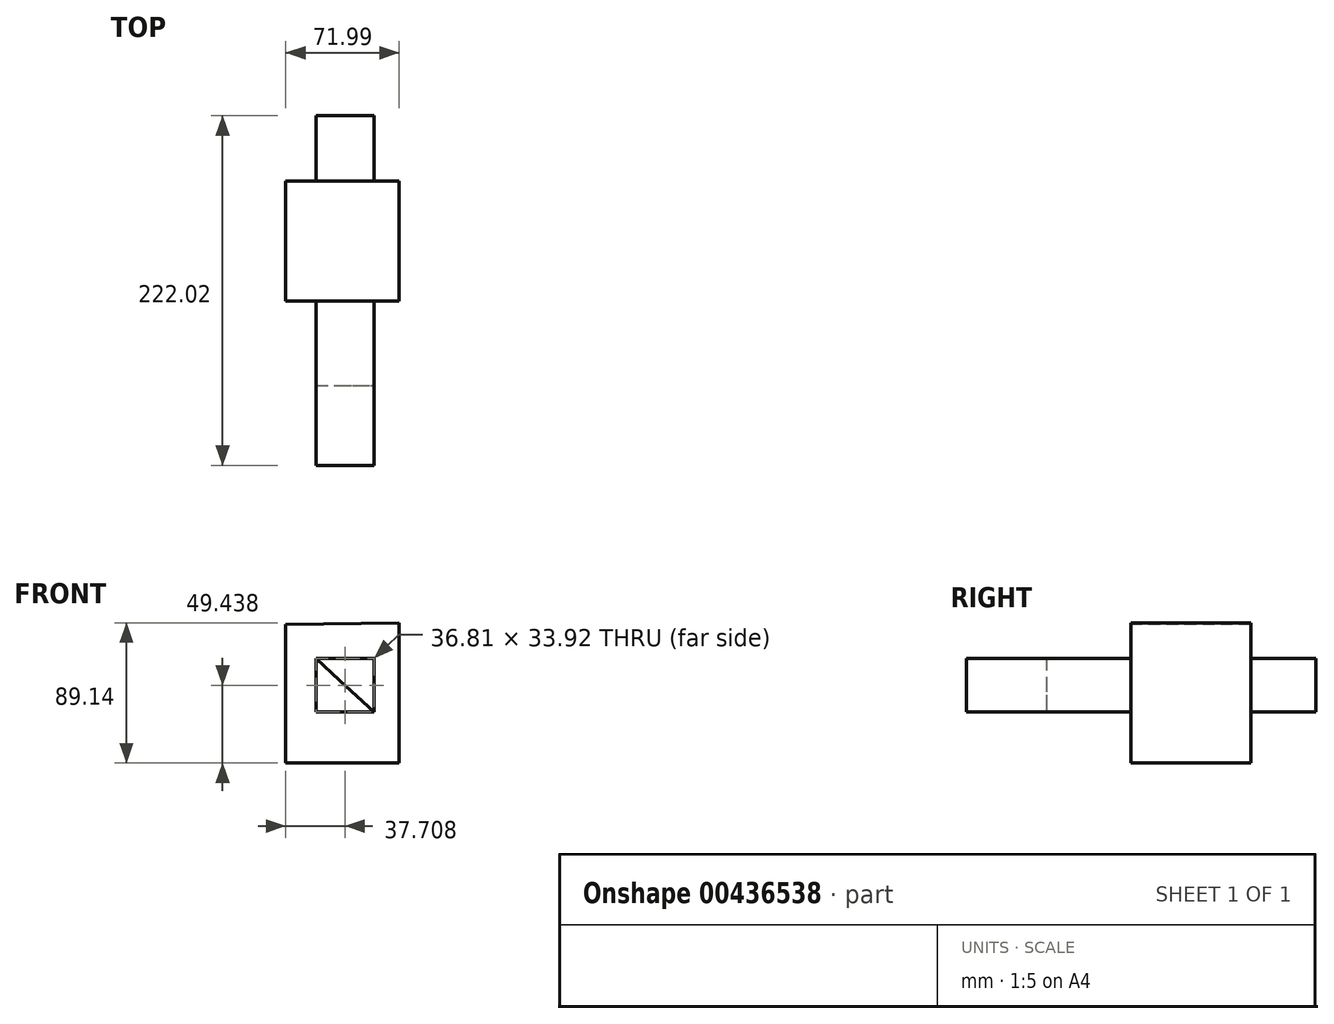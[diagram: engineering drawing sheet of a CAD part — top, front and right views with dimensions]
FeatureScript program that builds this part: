
annotation { "Feature Type Name" : "Feature", "Feature Type Description" : "" }
export const myFeature = defineFeature(function(context is Context, id is Id, definition is map)
    precondition{}
    {
        {
            var Q0;
            Q0=qCreatedBy(makeId("Front.planeOp"),FACE);
            var sketch = newSketch(context, id + "F0", { "sketchPlane" : qUnion([Q0])});
            skLineSegment(sketch, "E0", {"start": v(-34.28, 41.86) * mm, "end": v(-34.28, -46.37) * mm});
            skLineSegment(sketch, "E1", {"start": v(-34.28, -46.37) * mm, "end": v(37.71, -46.37) * mm});
            skLineSegment(sketch, "E2", {"start": v(37.71, -46.37) * mm, "end": v(37.71, 42.77) * mm});
            skLineSegment(sketch, "E3", {"start": v(37.71, 42.77) * mm, "end": v(-34.28, 41.86) * mm});
            skSolve(sketch);
        }
        {
            var Q0;
            Q0 = qSketchRegion(id + "F0", true);
            extrude(context, id + "F1", {"entities" : qUnion([Q0]), "depth" : -50.8 * mm});
        }
        {
            var Q0;
            Q0=makeQuery(id+"F1.opExtrude","CAP_FACE",FACE,{"disambiguationData":[OSD([sQuery(id+"F0.wireOp",EDGE,"E0"),sQuery(id+"F0.wireOp",EDGE,"E1"),sQuery(id+"F0.wireOp",EDGE,"E2"),sQuery(id+"F0.wireOp",EDGE,"E3")])],"isStart":false});
            extrude(context, id + "F2", {"entities" : qUnion([Q0]), "operationType" : NewBodyOperationType.ADD, "depth" : 25.4 * mm});
        }
        {
            var Q0;
            Q0=makeQuery(id+"F1.opExtrude","CAP_FACE",FACE,{"disambiguationData":[OSD([sQuery(id+"F0.wireOp",EDGE,"E0"),sQuery(id+"F0.wireOp",EDGE,"E1"),sQuery(id+"F0.wireOp",EDGE,"E2"),sQuery(id+"F0.wireOp",EDGE,"E3")])],"isStart":true});
            var sketch = newSketch(context, id + "F3", { "sketchPlane" : qUnion([Q0])});
            skSolve(sketch);
        }
        {
            var Q0;
            Q0=makeQuery(id+"F3.imprint","IMPRINT",FACE,{"disambiguationData":[TD([[makeQuery(id+"F3.imprint","IMPRINT",EDGE,{"derivedFrom":makeQuery(id+"F1.opExtrude","CAP_EDGE",EDGE,{"disambiguationData":[OSD([sQuery(id+"F0.wireOp",EDGE,"E0")])],"isStart":true})}),1.0]])]});
            var sketch = newSketch(context, id + "F4", { "sketchPlane" : qUnion([Q0])});
            skLineSegment(sketch, "E4.bottom", {"start": v(-14.98, 20.03) * mm, "end": v(21.83, 20.03) * mm});
            skLineSegment(sketch, "E4.top", {"start": v(-14.98, -13.9) * mm, "end": v(21.83, -13.9) * mm});
            skLineSegment(sketch, "E4.left", {"start": v(-14.98, 20.03) * mm, "end": v(-14.98, -13.9) * mm});
            skLineSegment(sketch, "E4.right", {"start": v(21.83, 20.03) * mm, "end": v(21.83, -13.9) * mm});
            skSolve(sketch);
        }
        {
            var Q0;
            Q0 = qSketchRegion(id + "F3", true);
            var sketch = newSketch(context, id + "F5", { "sketchPlane" : qUnion([Q0])});
            skSolve(sketch);
        }
        {
            var Q0;
            Q0=makeQuery(id+"F4.imprint","IMPRINT",FACE,{"disambiguationData":[TD([[makeQuery(id+"F4.imprint","IMPRINT",EDGE,{"derivedFrom":sQuery(id+"F4.wireOp",EDGE,"E4.bottom")}),-1.0]])]});
            extrude(context, id + "F6", {"entities" : qUnion([Q0]), "operationType" : NewBodyOperationType.ADD, "oppositeDirection" : true, "depth" : 117.7 * mm});
        }
        {
            var Q0;
            Q0 = qSketchRegion(id + "F4", true);
            var Q1;
            Q1=makeQuery(id+"F4.imprint","IMPRINT",FACE,{"disambiguationData":[TD([[makeQuery(id+"F4.imprint","IMPRINT",EDGE,{"derivedFrom":sQuery(id+"F4.wireOp",EDGE,"E4.bottom")}),-1.0]])]});
            var Q2;
            Q2 = qSketchRegion(id + "F5", true);
            extrude(context, id + "F7", {"entities" : qUnion([Q0, Q1, Q2]), "operationType" : NewBodyOperationType.ADD, "depth" : 53.5 * mm, "offsetDistance" : 25.4 * mm});
        }
        {
            var Q0;
            Q0=makeQuery(id+"F7.opExtrude","CAP_FACE",FACE,{"disambiguationData":[OSD([sQuery(id+"F4.wireOp",EDGE,"E4.bottom"),sQuery(id+"F4.wireOp",EDGE,"E4.top"),sQuery(id+"F4.wireOp",EDGE,"E4.left"),sQuery(id+"F4.wireOp",EDGE,"E4.right")])],"isStart":false});
            var sketch = newSketch(context, id + "F8", { "sketchPlane" : qUnion([Q0])});
            skLineSegment(sketch, "E5", {"start": v(0, 6.3) * mm, "end": v(21.83, -13.9) * mm});
            skLineSegment(sketch, "E6", {"start": v(-14.98, 20.03) * mm, "end": v(0, 6.3) * mm});
            skSolve(sketch);
        }
        {
            var Q0;
            Q0=makeQuery(id+"F8.imprint","IMPRINT",FACE,{"disambiguationData":[TD([[makeQuery(id+"F8.imprint","IMPRINT",EDGE,{"derivedFrom":sQuery(id+"F8.wireOp",EDGE,"E5")}),1.0]])]});
            extrude(context, id + "F9", {"entities" : qUnion([Q0]), "operationType" : NewBodyOperationType.ADD, "depth" : 50.8 * mm, "offsetDistance" : 25.4 * mm});
        }
    });
